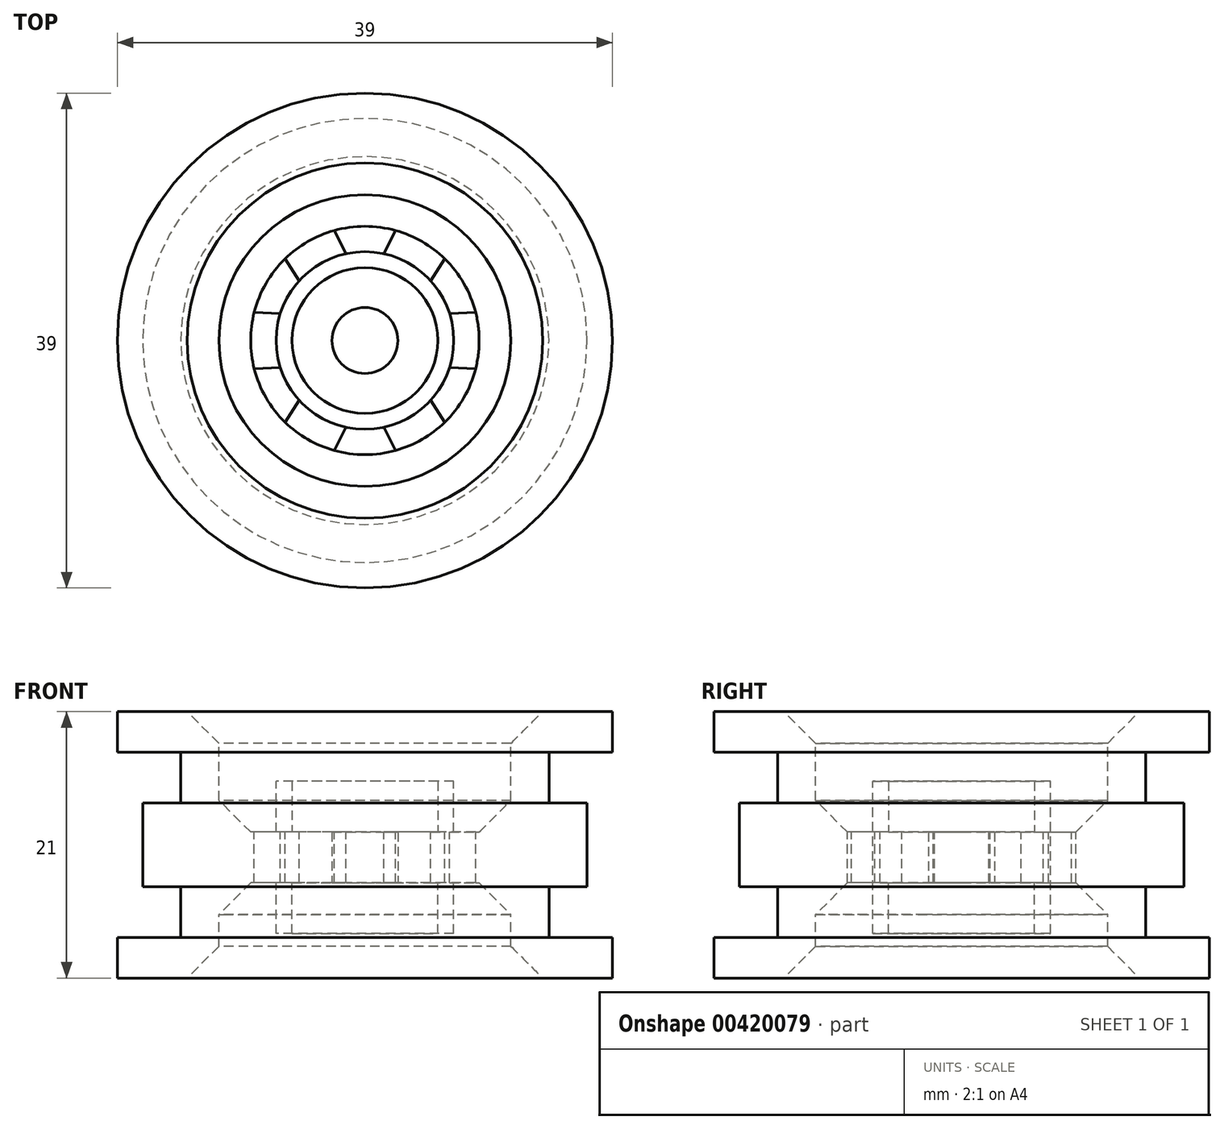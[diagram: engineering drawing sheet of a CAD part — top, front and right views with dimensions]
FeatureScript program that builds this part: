
annotation { "Feature Type Name" : "Feature", "Feature Type Description" : "" }
export const myFeature = defineFeature(function(context is Context, id is Id, definition is map)
    precondition{}
    {
        {
            var Q0;
            Q0=qCreatedBy(makeId("Front.planeOp"),FACE);
            var sketch = newSketch(context, id + "F0", { "sketchPlane" : qUnion([Q0])});
            skLineSegment(sketch, "E0", {"start": v(0, 0) * mm, "end": v(0, -21) * mm, "construction": true});
            skLineSegment(sketch, "E1", {"start": v(0, 0) * mm, "end": v(19.5, 0) * mm});
            skLineSegment(sketch, "E2", {"start": v(19.5, 0) * mm, "end": v(19.5, -3.2) * mm});
            skLineSegment(sketch, "E3", {"start": v(19.5, -3.2) * mm, "end": v(14.5, -3.2) * mm});
            skLineSegment(sketch, "E4", {"start": v(14.5, -3.2) * mm, "end": v(14.5, -7.2) * mm});
            skLineSegment(sketch, "E5", {"start": v(14.5, -7.2) * mm, "end": v(17.5, -7.2) * mm});
            skLineSegment(sketch, "E6", {"start": v(17.5, -7.2) * mm, "end": v(17.5, -13.8) * mm});
            skLineSegment(sketch, "E7", {"start": v(17.5, -13.8) * mm, "end": v(14.5, -13.8) * mm});
            skLineSegment(sketch, "E8", {"start": v(14.5, -13.8) * mm, "end": v(14.5, -17.8) * mm});
            skLineSegment(sketch, "E9", {"start": v(14.5, -17.8) * mm, "end": v(19.5, -17.8) * mm});
            skLineSegment(sketch, "E10", {"start": v(19.5, -17.8) * mm, "end": v(19.5, -21) * mm});
            skLineSegment(sketch, "E11", {"start": v(19.5, -21) * mm, "end": v(0, -21) * mm});
            skLineSegment(sketch, "E12", {"start": v(0, 0) * mm, "end": v(0, -21) * mm});
            skLineSegment(sketch, "E13", {"start": v(14, 0) * mm, "end": v(11.5, -2.5) * mm});
            skLineSegment(sketch, "E14", {"start": v(11.5, -2.5) * mm, "end": v(11.5, -9.5) * mm});
            skLineSegment(sketch, "E15", {"start": v(11.5, -9.5) * mm, "end": v(0, -9.5) * mm});
            skLineSegment(sketch, "E16", {"start": v(0, -13.5) * mm, "end": v(11.5, -13.5) * mm});
            skLineSegment(sketch, "E17", {"start": v(11.5, -13.5) * mm, "end": v(11.5, -18.5) * mm});
            skLineSegment(sketch, "E18", {"start": v(11.5, -18.5) * mm, "end": v(14, -21) * mm});
            skLineSegment(sketch, "E19", {"start": v(9, -9.5) * mm, "end": v(11.5, -7) * mm});
            skLineSegment(sketch, "E20", {"start": v(9, -13.5) * mm, "end": v(11.5, -16) * mm});
            skSolve(sketch);
        }
        {
            var Q0;
            {var subQ1=sQuery(id+"F0.wireOp",EDGE,"E2");Q0=makeQuery(id+"F0.imprint","IMPRINT",FACE,{"disambiguationData":[TD([[makeQuery(id+"F0.imprint","IMPRINT",EDGE,{"derivedFrom":subQ1}),-1.0]])]});}
            var Q1;
            {var subQ3=sQuery(id+"F0.wireOp",EDGE,"E19");Q1=makeQuery(id+"F0.imprint","IMPRINT",FACE,{"disambiguationData":[TD([[makeQuery(id+"F0.imprint","IMPRINT",EDGE,{"derivedFrom":subQ3}),-1.0]])]});}
            var Q2;
            {var subQ3=sQuery(id+"F0.wireOp",EDGE,"E20");Q2=makeQuery(id+"F0.imprint","IMPRINT",FACE,{"disambiguationData":[TD([[makeQuery(id+"F0.imprint","IMPRINT",EDGE,{"derivedFrom":subQ3}),1.0]])]});}
            var Q3;
            Q3=sQuery(id+"F0.wireOp",EDGE,"E12");
            revolve(context, id + "F1", {"entities" : qUnion([Q0, Q1, Q2]), "axis" : qUnion([Q3]), "revolveType" : RevolveType.FULL});
        }
        {
            var Q0;
            Q0=makeQuery(id+"F1.opRevolve","SWEPT_FACE",FACE,{"disambiguationData":[OSD([sQuery(id+"F0.wireOp",EDGE,"E15")])]});
            var sketch = newSketch(context, id + "F2", { "sketchPlane" : qUnion([Q0])});
            skLineSegment(sketch, "E21", {"start": v(0, 4) * mm, "end": v(3.37, 10.47) * mm});
            skCircle(sketch, "E22", {"center": v(0, 0) * mm, "radius": 11 * mm, "construction": true});
            skLineSegment(sketch, "E23", {"start": v(0, 4) * mm, "end": v(-3.37, 10.47) * mm});
            skArc(sketch, "E24", {"start": v(3.37, 10.47) * mm, "mid": v(0, 11) * mm, "end": v(-3.37, 10.47) * mm});
            skArc(sketch, "E25.1.0", {"start": v(-10.75, -2.32) * mm, "mid": v(-9.53, -5.5) * mm, "end": v(-7.38, -8.15) * mm});
            skLineSegment(sketch, "E25.1.1", {"start": v(-3.46, -2) * mm, "end": v(-7.38, -8.15) * mm});
            skLineSegment(sketch, "E25.1.2", {"start": v(-3.46, -2) * mm, "end": v(-10.75, -2.32) * mm});
            skArc(sketch, "E25.2.0", {"start": v(7.38, -8.15) * mm, "mid": v(9.53, -5.5) * mm, "end": v(10.75, -2.32) * mm});
            skLineSegment(sketch, "E25.2.1", {"start": v(3.46, -2) * mm, "end": v(10.75, -2.32) * mm});
            skLineSegment(sketch, "E25.2.2", {"start": v(3.46, -2) * mm, "end": v(7.38, -8.15) * mm});
            skLineSegment(sketch, "E26.MirrorCS", {"start": v(0, -4) * mm, "end": v(-3.37, -10.47) * mm});
            skLineSegment(sketch, "E27.MirrorCS", {"start": v(0, -4) * mm, "end": v(3.37, -10.47) * mm});
            skArc(sketch, "E28.MirrorCS", {"start": v(3.37, -10.47) * mm, "mid": v(0, -11) * mm, "end": v(-3.37, -10.47) * mm});
            skLineSegment(sketch, "E29.1.0", {"start": v(3.46, 2) * mm, "end": v(7.38, 8.15) * mm});
            skArc(sketch, "E29.1.1", {"start": v(7.38, 8.15) * mm, "mid": v(9.53, 5.5) * mm, "end": v(10.75, 2.32) * mm});
            skLineSegment(sketch, "E29.1.2", {"start": v(3.46, 2) * mm, "end": v(10.75, 2.32) * mm});
            skLineSegment(sketch, "E29.2.0", {"start": v(-3.46, 2) * mm, "end": v(-10.75, 2.32) * mm});
            skArc(sketch, "E29.2.1", {"start": v(-10.75, 2.32) * mm, "mid": v(-9.53, 5.5) * mm, "end": v(-7.38, 8.15) * mm});
            skLineSegment(sketch, "E29.2.2", {"start": v(-3.46, 2) * mm, "end": v(-7.38, 8.15) * mm});
            skCircle(sketch, "E30", {"center": v(0, 0) * mm, "radius": 7 * mm});
            skSolve(sketch);
        }
        {
            var Q0;
            {var subQ0=sQuery(id+"F2.wireOp",EDGE,"E30");var subQ1=sQuery(id+"F2.wireOp",EDGE,"E29.2.0");var subQ2=makeQuery(id+"F2.imprint","INTERSECT",VERTEX,{"derivedFrom":[subQ1,subQ0]});Q0=makeQuery(id+"F2.imprint","IMPRINT",FACE,{"disambiguationData":[TD([[makeQuery(id+"F2.imprint","IMPRINT",EDGE,{"disambiguationData":[TD([[subQ2,1.0]])],"derivedFrom":subQ0}),-1.0]])]});}
            var Q1;
            {var subQ0=sQuery(id+"F2.wireOp",EDGE,"E30");var subQ1=sQuery(id+"F2.wireOp",EDGE,"E21");var subQ2=makeQuery(id+"F2.imprint","INTERSECT",VERTEX,{"derivedFrom":[subQ1,subQ0]});Q1=makeQuery(id+"F2.imprint","IMPRINT",FACE,{"disambiguationData":[TD([[makeQuery(id+"F2.imprint","IMPRINT",EDGE,{"disambiguationData":[TD([[subQ2,-1.0]])],"derivedFrom":subQ0}),-1.0]])]});}
            var Q2;
            {var subQ0=sQuery(id+"F2.wireOp",EDGE,"E30");var subQ1=sQuery(id+"F2.wireOp",EDGE,"E29.1.0");var subQ2=makeQuery(id+"F2.imprint","INTERSECT",VERTEX,{"derivedFrom":[subQ1,subQ0]});Q2=makeQuery(id+"F2.imprint","IMPRINT",FACE,{"disambiguationData":[TD([[makeQuery(id+"F2.imprint","IMPRINT",EDGE,{"disambiguationData":[TD([[subQ2,1.0]])],"derivedFrom":subQ0}),-1.0]])]});}
            var Q3;
            {var subQ0=sQuery(id+"F2.wireOp",EDGE,"E30");var subQ1=sQuery(id+"F2.wireOp",EDGE,"E25.2.1");var subQ2=makeQuery(id+"F2.imprint","INTERSECT",VERTEX,{"derivedFrom":[subQ1,subQ0]});Q3=makeQuery(id+"F2.imprint","IMPRINT",FACE,{"disambiguationData":[TD([[makeQuery(id+"F2.imprint","IMPRINT",EDGE,{"disambiguationData":[TD([[subQ2,1.0]])],"derivedFrom":subQ0}),-1.0]])]});}
            var Q4;
            {var subQ0=sQuery(id+"F2.wireOp",EDGE,"E30");var subQ1=sQuery(id+"F2.wireOp",EDGE,"E26.MirrorCS");var subQ2=makeQuery(id+"F2.imprint","INTERSECT",VERTEX,{"derivedFrom":[subQ1,subQ0]});Q4=makeQuery(id+"F2.imprint","IMPRINT",FACE,{"disambiguationData":[TD([[makeQuery(id+"F2.imprint","IMPRINT",EDGE,{"disambiguationData":[TD([[subQ2,-1.0]])],"derivedFrom":subQ0}),-1.0]])]});}
            var Q5;
            {var subQ0=sQuery(id+"F2.wireOp",EDGE,"E30");var subQ1=sQuery(id+"F2.wireOp",EDGE,"E25.1.1");var subQ2=makeQuery(id+"F2.imprint","INTERSECT",VERTEX,{"derivedFrom":[subQ1,subQ0]});Q5=makeQuery(id+"F2.imprint","IMPRINT",FACE,{"disambiguationData":[TD([[makeQuery(id+"F2.imprint","IMPRINT",EDGE,{"disambiguationData":[TD([[subQ2,1.0]])],"derivedFrom":subQ0}),-1.0]])]});}
            extrude(context, id + "F3", {"entities" : qUnion([Q0, Q1, Q2, Q3, Q4, Q5]), "operationType" : NewBodyOperationType.REMOVE, "endBound" : BoundingType.THROUGH_ALL, "oppositeDirection" : true, "depth" : 25 * mm});
        }
        {
            var Q0;
            Q0=makeQuery(id+"F1.opRevolve","SWEPT_FACE",FACE,{"disambiguationData":[OSD([sQuery(id+"F0.wireOp",EDGE,"E15")])]});
            var sketch = newSketch(context, id + "F4", { "sketchPlane" : qUnion([Q0])});
            skCircle(sketch, "E31", {"center": v(0, 0) * mm, "radius": 5.75 * mm});
            skCircle(sketch, "E32", {"center": v(0, 0) * mm, "radius": 7 * mm});
            skSolve(sketch);
        }
        {
            var Q0;
            Q0=makeQuery(id+"F4.imprint","IMPRINT",FACE,{"disambiguationData":[TD([[makeQuery(id+"F4.imprint","IMPRINT",EDGE,{"derivedFrom":sQuery(id+"F4.wireOp",EDGE,"E31")}),-1.0]])]});
            extrude(context, id + "F5", {"entities" : qUnion([Q0]), "operationType" : NewBodyOperationType.ADD, "depth" : 4 * mm});
        }
        {
            var Q0;
            Q0=makeQuery(id+"F1.opRevolve","SWEPT_FACE",FACE,{"disambiguationData":[OSD([sQuery(id+"F0.wireOp",EDGE,"E16")])]});
            var sketch = newSketch(context, id + "F6", { "sketchPlane" : qUnion([Q0])});
            skCircle(sketch, "E33", {"center": v(0, 0) * mm, "radius": 7 * mm});
            skCircle(sketch, "E34", {"center": v(0, 0) * mm, "radius": 5.75 * mm});
            skSolve(sketch);
        }
        {
            var Q0;
            Q0 = qSketchRegion(id + "F6", true);
            extrude(context, id + "F7", {"entities" : qUnion([Q0]), "operationType" : NewBodyOperationType.ADD, "depth" : 4 * mm});
        }
        {
            var Q0;
            Q0=makeQuery(id+"F7.boolean.opBoolean","SPLIT",FACE,{"disambiguationData":[TD([makeQuery(id+"F7.opExtrude","SWEPT_FACE",FACE,{"disambiguationData":[OSD([sQuery(id+"F6.wireOp",EDGE,"E34")])]})])],"derivedFrom":makeQuery(id+"F1.opRevolve","SWEPT_FACE",FACE,{"disambiguationData":[OSD([sQuery(id+"F0.wireOp",EDGE,"E16")])]})});
            var sketch = newSketch(context, id + "F8", { "sketchPlane" : qUnion([Q0])});
            skCircle(sketch, "E35", {"center": v(0, 0) * mm, "radius": 2.6 * mm});
            skSolve(sketch);
        }
        {
            var Q0;
            Q0 = qSketchRegion(id + "F8", true);
            extrude(context, id + "F9", {"entities" : qUnion([Q0]), "operationType" : NewBodyOperationType.REMOVE, "endBound" : BoundingType.THROUGH_ALL, "oppositeDirection" : true, "depth" : 25 * mm});
        }
    });
